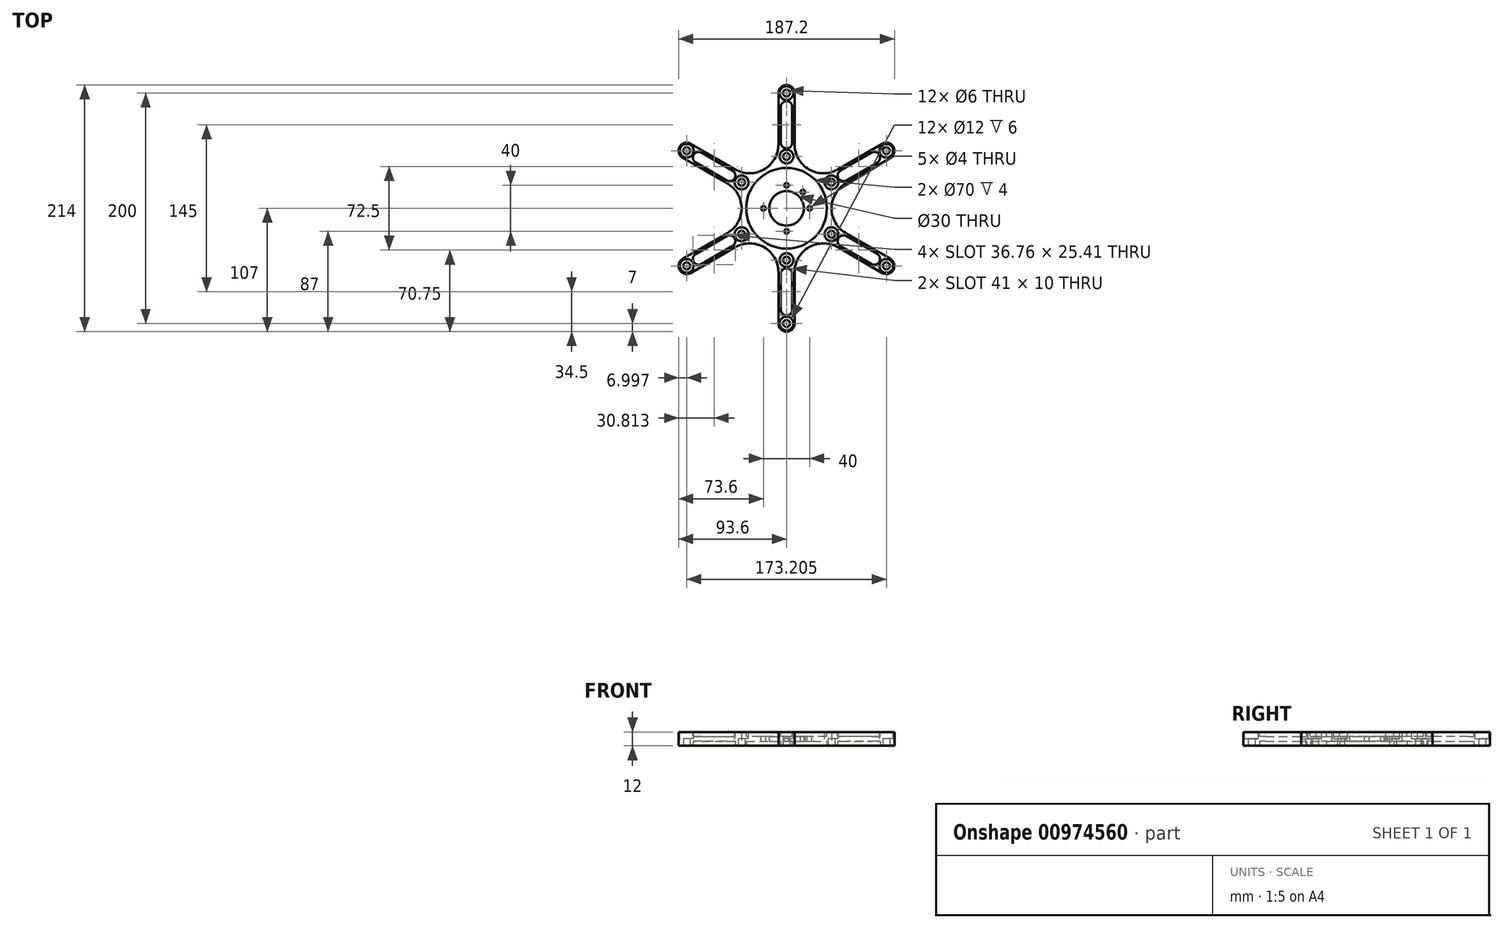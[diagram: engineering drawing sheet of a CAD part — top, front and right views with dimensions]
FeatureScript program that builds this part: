
annotation { "Feature Type Name" : "Feature", "Feature Type Description" : "" }
export const myFeature = defineFeature(function(context is Context, id is Id, definition is map)
    precondition{}
    {
        {
            var Q0;
            Q0=qCreatedBy(makeId("Top.planeOp"),FACE);
            var sketch = newSketch(context, id + "F0", { "sketchPlane" : qUnion([Q0])});
            skLineSegment(sketch, "E0", {"start": v(0, 0) * mm, "end": v(0, 90) * mm, "construction": true});
            skCircle(sketch, "E1", {"center": v(0, 100) * mm, "radius": 3 * mm});
            skCircle(sketch, "E2", {"center": v(0, 45) * mm, "radius": 3 * mm});
            skArc(sketch, "E3", {"start": v(7, 100) * mm, "mid": v(0, 107) * mm, "end": v(-7, 100) * mm});
            skLineSegment(sketch, "E4", {"start": v(-7, 100) * mm, "end": v(-7, 55.43) * mm});
            skLineSegment(sketch, "E5", {"start": v(7, 100) * mm, "end": v(7, 55.43) * mm});
            skLineSegment(sketch, "E6.1.0", {"start": v(-90.1, 43.94) * mm, "end": v(-51.5, 21.65) * mm});
            skCircle(sketch, "E6.1.1", {"center": v(-86.6, 50) * mm, "radius": 3 * mm});
            skCircle(sketch, "E6.1.2", {"center": v(-38.97, 22.5) * mm, "radius": 3 * mm});
            skArc(sketch, "E6.1.3", {"start": v(-83.1, 56.06) * mm, "mid": v(-92.66, 53.5) * mm, "end": v(-90.1, 43.94) * mm});
            skLineSegment(sketch, "E6.1.4", {"start": v(-83.1, 56.06) * mm, "end": v(-44.5, 33.77) * mm});
            skLineSegment(sketch, "E6.2.0", {"start": v(-83.1, -56.06) * mm, "end": v(-44.5, -33.77) * mm});
            skCircle(sketch, "E6.2.1", {"center": v(-86.6, -50) * mm, "radius": 3 * mm});
            skCircle(sketch, "E6.2.2", {"center": v(-38.97, -22.5) * mm, "radius": 3 * mm});
            skArc(sketch, "E6.2.3", {"start": v(-90.1, -43.94) * mm, "mid": v(-92.66, -53.5) * mm, "end": v(-83.1, -56.06) * mm});
            skLineSegment(sketch, "E6.2.4", {"start": v(-90.1, -43.94) * mm, "end": v(-51.5, -21.65) * mm});
            skLineSegment(sketch, "E6.3.0", {"start": v(7, -100) * mm, "end": v(7, -55.43) * mm});
            skCircle(sketch, "E6.3.1", {"center": v(0, -100) * mm, "radius": 3 * mm});
            skCircle(sketch, "E6.3.2", {"center": v(0, -45) * mm, "radius": 3 * mm});
            skArc(sketch, "E6.3.3", {"start": v(-7, -100) * mm, "mid": v(0, -107) * mm, "end": v(7, -100) * mm});
            skLineSegment(sketch, "E6.3.4", {"start": v(-7, -100) * mm, "end": v(-7, -55.43) * mm});
            skLineSegment(sketch, "E6.4.0", {"start": v(90.1, -43.94) * mm, "end": v(51.5, -21.65) * mm});
            skCircle(sketch, "E6.4.1", {"center": v(86.6, -50) * mm, "radius": 3 * mm});
            skCircle(sketch, "E6.4.2", {"center": v(38.97, -22.5) * mm, "radius": 3 * mm});
            skArc(sketch, "E6.4.3", {"start": v(83.1, -56.06) * mm, "mid": v(92.66, -53.5) * mm, "end": v(90.1, -43.94) * mm});
            skLineSegment(sketch, "E6.4.4", {"start": v(83.1, -56.06) * mm, "end": v(44.5, -33.77) * mm});
            skLineSegment(sketch, "E6.5.0", {"start": v(83.1, 56.06) * mm, "end": v(44.5, 33.77) * mm});
            skCircle(sketch, "E6.5.1", {"center": v(86.6, 50) * mm, "radius": 3 * mm});
            skCircle(sketch, "E6.5.2", {"center": v(38.97, 22.5) * mm, "radius": 3 * mm});
            skArc(sketch, "E6.5.3", {"start": v(90.1, 43.94) * mm, "mid": v(92.66, 53.5) * mm, "end": v(83.1, 56.06) * mm});
            skLineSegment(sketch, "E6.5.4", {"start": v(90.1, 43.94) * mm, "end": v(51.5, 21.65) * mm});
            skPoint(sketch, "E6.center", {"position": v(0, 0) * mm});
            skArc(sketch, "E7", {"start": v(7, 55.43) * mm, "mid": v(19.5, 33.77) * mm, "end": v(44.5, 33.77) * mm});
            skArc(sketch, "E8", {"start": v(-44.5, 33.77) * mm, "mid": v(-19.5, 33.77) * mm, "end": v(-7, 55.43) * mm});
            skArc(sketch, "E9", {"start": v(-51.5, -21.65) * mm, "mid": v(-39, 0) * mm, "end": v(-51.5, 21.65) * mm});
            skArc(sketch, "E10", {"start": v(-7, -55.43) * mm, "mid": v(-19.5, -33.77) * mm, "end": v(-44.5, -33.77) * mm});
            skArc(sketch, "E11", {"start": v(44.5, -33.77) * mm, "mid": v(19.5, -33.77) * mm, "end": v(7, -55.43) * mm});
            skArc(sketch, "E12", {"start": v(51.5, 21.65) * mm, "mid": v(39, 0) * mm, "end": v(51.5, -21.65) * mm});
            skLineSegment(sketch, "E13.trimOffspring", {"start": v(7, 12.12) * mm, "end": v(4.3, 10.57) * mm, "construction": true});
            skLineSegment(sketch, "E14.trimOffspring", {"start": v(7, 12.12) * mm, "end": v(7, 11.88) * mm, "construction": true});
            skLineSegment(sketch, "E15.trimOffspring", {"start": v(-7, 12.12) * mm, "end": v(-7, 9) * mm, "construction": true});
            skLineSegment(sketch, "E16.trimOffspring", {"start": v(-7, 12.12) * mm, "end": v(-6.8, 12) * mm, "construction": true});
            skLineSegment(sketch, "E17.trimOffspring", {"start": v(-14, 0) * mm, "end": v(-11.3, -1.56) * mm, "construction": true});
            skLineSegment(sketch, "E18.trimOffspring", {"start": v(-14, 0) * mm, "end": v(-13.8, 0.12) * mm, "construction": true});
            skLineSegment(sketch, "E19.trimOffspring", {"start": v(-7, -12.12) * mm, "end": v(-4.3, -10.57) * mm, "construction": true});
            skLineSegment(sketch, "E20.trimOffspring", {"start": v(-7, -12.12) * mm, "end": v(-7, -11.88) * mm, "construction": true});
            skLineSegment(sketch, "E21.trimOffspring", {"start": v(7, -12.12) * mm, "end": v(7, -9) * mm, "construction": true});
            skLineSegment(sketch, "E22.trimOffspring", {"start": v(7, -12.12) * mm, "end": v(6.8, -12) * mm, "construction": true});
            skLineSegment(sketch, "E23.trimOffspring", {"start": v(14, 0) * mm, "end": v(11.3, 1.56) * mm, "construction": true});
            skLineSegment(sketch, "E24.trimOffspring", {"start": v(14, 0) * mm, "end": v(13.8, -0.12) * mm, "construction": true});
            skCircle(sketch, "E25", {"center": v(0, 0) * mm, "radius": 15 * mm});
            skSolve(sketch);
        }
        {
            var Q0;
            Q0=qSketchRegion(id+"F0",true);
            extrude(context, id + "F1", {"entities" : qUnion([Q0]), "depth" : 12 * mm, "offsetDistance" : 25 * mm});
        }
        {
            var Q0;
            Q0=makeQuery(id+"F1.opExtrude","CAP_FACE",FACE,{"disambiguationData":[OSD([sQuery(id+"F0.wireOp",EDGE,"E1"),sQuery(id+"F0.wireOp",EDGE,"E2"),sQuery(id+"F0.wireOp",EDGE,"E3"),sQuery(id+"F0.wireOp",EDGE,"E4"),sQuery(id+"F0.wireOp",EDGE,"E5"),sQuery(id+"F0.wireOp",EDGE,"E6.1.0"),sQuery(id+"F0.wireOp",EDGE,"E6.1.1"),sQuery(id+"F0.wireOp",EDGE,"E6.1.2"),sQuery(id+"F0.wireOp",EDGE,"E6.1.3"),sQuery(id+"F0.wireOp",EDGE,"E6.1.4"),sQuery(id+"F0.wireOp",EDGE,"E6.2.0"),sQuery(id+"F0.wireOp",EDGE,"E6.2.1"),sQuery(id+"F0.wireOp",EDGE,"E6.2.2"),sQuery(id+"F0.wireOp",EDGE,"E6.2.3"),sQuery(id+"F0.wireOp",EDGE,"E6.2.4"),sQuery(id+"F0.wireOp",EDGE,"E6.3.0"),sQuery(id+"F0.wireOp",EDGE,"E6.3.1"),sQuery(id+"F0.wireOp",EDGE,"E6.3.2"),sQuery(id+"F0.wireOp",EDGE,"E6.3.3"),sQuery(id+"F0.wireOp",EDGE,"E6.3.4"),sQuery(id+"F0.wireOp",EDGE,"E6.4.0"),sQuery(id+"F0.wireOp",EDGE,"E6.4.1"),sQuery(id+"F0.wireOp",EDGE,"E6.4.2"),sQuery(id+"F0.wireOp",EDGE,"E6.4.3"),sQuery(id+"F0.wireOp",EDGE,"E6.4.4"),sQuery(id+"F0.wireOp",EDGE,"E6.5.0"),sQuery(id+"F0.wireOp",EDGE,"E6.5.1"),sQuery(id+"F0.wireOp",EDGE,"E6.5.2"),sQuery(id+"F0.wireOp",EDGE,"E6.5.3"),sQuery(id+"F0.wireOp",EDGE,"E6.5.4"),sQuery(id+"F0.wireOp",EDGE,"E7"),sQuery(id+"F0.wireOp",EDGE,"E8"),sQuery(id+"F0.wireOp",EDGE,"E9"),sQuery(id+"F0.wireOp",EDGE,"E10"),sQuery(id+"F0.wireOp",EDGE,"E11"),sQuery(id+"F0.wireOp",EDGE,"E12")])],"isStart":false});
            var sketch = newSketch(context, id + "F2", { "sketchPlane" : qUnion([Q0])});
            skCircle(sketch, "E26", {"center": v(-86.6, 50) * mm, "radius": 6 * mm});
            skCircle(sketch, "E27", {"center": v(0, 100) * mm, "radius": 6 * mm});
            skCircle(sketch, "E28", {"center": v(86.6, 50) * mm, "radius": 6 * mm});
            skCircle(sketch, "E29", {"center": v(86.6, -50) * mm, "radius": 6 * mm});
            skCircle(sketch, "E30", {"center": v(0, -100) * mm, "radius": 6 * mm});
            skCircle(sketch, "E31", {"center": v(-86.6, -50) * mm, "radius": 6 * mm});
            skCircle(sketch, "E32", {"center": v(-38.97, 22.5) * mm, "radius": 6 * mm});
            skCircle(sketch, "E33", {"center": v(0, 45) * mm, "radius": 6 * mm});
            skCircle(sketch, "E34", {"center": v(38.97, 22.5) * mm, "radius": 6 * mm});
            skCircle(sketch, "E35", {"center": v(38.97, -22.5) * mm, "radius": 6 * mm});
            skCircle(sketch, "E36", {"center": v(0, -45) * mm, "radius": 6 * mm});
            skCircle(sketch, "E37", {"center": v(-38.97, -22.5) * mm, "radius": 6 * mm});
            skSolve(sketch);
        }
        {
            var Q0;
            Q0 = qSketchRegion(id + "F2", true);
            extrude(context, id + "F3", {"entities" : qUnion([Q0]), "operationType" : NewBodyOperationType.REMOVE, "oppositeDirection" : true, "depth" : 6 * mm, "offsetDistance" : 25 * mm});
        }
        {
            var Q0;
            Q0=makeQuery(id+"F1.opExtrude","CAP_FACE",FACE,{"disambiguationData":[OSD([sQuery(id+"F0.wireOp",EDGE,"E1"),sQuery(id+"F0.wireOp",EDGE,"E2"),sQuery(id+"F0.wireOp",EDGE,"E3"),sQuery(id+"F0.wireOp",EDGE,"E4"),sQuery(id+"F0.wireOp",EDGE,"E5"),sQuery(id+"F0.wireOp",EDGE,"E6.1.0"),sQuery(id+"F0.wireOp",EDGE,"E6.1.1"),sQuery(id+"F0.wireOp",EDGE,"E6.1.2"),sQuery(id+"F0.wireOp",EDGE,"E6.1.3"),sQuery(id+"F0.wireOp",EDGE,"E6.1.4"),sQuery(id+"F0.wireOp",EDGE,"E6.2.0"),sQuery(id+"F0.wireOp",EDGE,"E6.2.1"),sQuery(id+"F0.wireOp",EDGE,"E6.2.2"),sQuery(id+"F0.wireOp",EDGE,"E6.2.3"),sQuery(id+"F0.wireOp",EDGE,"E6.2.4"),sQuery(id+"F0.wireOp",EDGE,"E6.3.0"),sQuery(id+"F0.wireOp",EDGE,"E6.3.1"),sQuery(id+"F0.wireOp",EDGE,"E6.3.2"),sQuery(id+"F0.wireOp",EDGE,"E6.3.3"),sQuery(id+"F0.wireOp",EDGE,"E6.3.4"),sQuery(id+"F0.wireOp",EDGE,"E6.4.0"),sQuery(id+"F0.wireOp",EDGE,"E6.4.1"),sQuery(id+"F0.wireOp",EDGE,"E6.4.2"),sQuery(id+"F0.wireOp",EDGE,"E6.4.3"),sQuery(id+"F0.wireOp",EDGE,"E6.4.4"),sQuery(id+"F0.wireOp",EDGE,"E6.5.0"),sQuery(id+"F0.wireOp",EDGE,"E6.5.1"),sQuery(id+"F0.wireOp",EDGE,"E6.5.2"),sQuery(id+"F0.wireOp",EDGE,"E6.5.3"),sQuery(id+"F0.wireOp",EDGE,"E6.5.4"),sQuery(id+"F0.wireOp",EDGE,"E7"),sQuery(id+"F0.wireOp",EDGE,"E8"),sQuery(id+"F0.wireOp",EDGE,"E9"),sQuery(id+"F0.wireOp",EDGE,"E10"),sQuery(id+"F0.wireOp",EDGE,"E11"),sQuery(id+"F0.wireOp",EDGE,"E12"),sQuery(id+"F0.wireOp",EDGE,"E25")])],"isStart":false});
            var sketch = newSketch(context, id + "F4", { "sketchPlane" : qUnion([Q0])});
            skCircle(sketch, "E38", {"center": v(0, 20) * mm, "radius": 2 * mm});
            skCircle(sketch, "E39.1.0", {"center": v(-20, 0) * mm, "radius": 2 * mm});
            skCircle(sketch, "E39.2.0", {"center": v(0, -20) * mm, "radius": 2 * mm});
            skCircle(sketch, "E39.3.0", {"center": v(20, 0) * mm, "radius": 2 * mm});
            skPoint(sketch, "E39.center", {"position": v(0, 0) * mm});
            skSolve(sketch);
        }
        {
            var Q0;
            Q0 = qSketchRegion(id + "F4", true);
            extrude(context, id + "F5", {"entities" : qUnion([Q0]), "operationType" : NewBodyOperationType.REMOVE, "endBound" : BoundingType.THROUGH_ALL, "oppositeDirection" : true, "depth" : 25 * mm, "offsetDistance" : 25 * mm});
        }
        {
            var Q0;
            Q0=makeQuery(id+"F1.opExtrude","CAP_FACE",FACE,{"disambiguationData":[OSD([sQuery(id+"F0.wireOp",EDGE,"E1"),sQuery(id+"F0.wireOp",EDGE,"E2"),sQuery(id+"F0.wireOp",EDGE,"E3"),sQuery(id+"F0.wireOp",EDGE,"E4"),sQuery(id+"F0.wireOp",EDGE,"E5"),sQuery(id+"F0.wireOp",EDGE,"E6.1.0"),sQuery(id+"F0.wireOp",EDGE,"E6.1.1"),sQuery(id+"F0.wireOp",EDGE,"E6.1.2"),sQuery(id+"F0.wireOp",EDGE,"E6.1.3"),sQuery(id+"F0.wireOp",EDGE,"E6.1.4"),sQuery(id+"F0.wireOp",EDGE,"E6.2.0"),sQuery(id+"F0.wireOp",EDGE,"E6.2.1"),sQuery(id+"F0.wireOp",EDGE,"E6.2.2"),sQuery(id+"F0.wireOp",EDGE,"E6.2.3"),sQuery(id+"F0.wireOp",EDGE,"E6.2.4"),sQuery(id+"F0.wireOp",EDGE,"E6.3.0"),sQuery(id+"F0.wireOp",EDGE,"E6.3.1"),sQuery(id+"F0.wireOp",EDGE,"E6.3.2"),sQuery(id+"F0.wireOp",EDGE,"E6.3.3"),sQuery(id+"F0.wireOp",EDGE,"E6.3.4"),sQuery(id+"F0.wireOp",EDGE,"E6.4.0"),sQuery(id+"F0.wireOp",EDGE,"E6.4.1"),sQuery(id+"F0.wireOp",EDGE,"E6.4.2"),sQuery(id+"F0.wireOp",EDGE,"E6.4.3"),sQuery(id+"F0.wireOp",EDGE,"E6.4.4"),sQuery(id+"F0.wireOp",EDGE,"E6.5.0"),sQuery(id+"F0.wireOp",EDGE,"E6.5.1"),sQuery(id+"F0.wireOp",EDGE,"E6.5.2"),sQuery(id+"F0.wireOp",EDGE,"E6.5.3"),sQuery(id+"F0.wireOp",EDGE,"E6.5.4"),sQuery(id+"F0.wireOp",EDGE,"E7"),sQuery(id+"F0.wireOp",EDGE,"E8"),sQuery(id+"F0.wireOp",EDGE,"E9"),sQuery(id+"F0.wireOp",EDGE,"E10"),sQuery(id+"F0.wireOp",EDGE,"E11"),sQuery(id+"F0.wireOp",EDGE,"E12"),sQuery(id+"F0.wireOp",EDGE,"E25")])],"isStart":false});
            var sketch = newSketch(context, id + "F6", { "sketchPlane" : qUnion([Q0])});
            skCircle(sketch, "E40", {"center": v(0, 0) * mm, "radius": 35 * mm});
            skLineSegment(sketch, "E41", {"start": v(0, 0) * mm, "end": v(0, 89.1) * mm, "construction": true});
            skLineSegment(sketch, "E42.bottom", {"start": v(0, 93) * mm, "end": v(0, 93) * mm});
            skLineSegment(sketch, "E42.top", {"start": v(0, 52) * mm, "end": v(0, 52) * mm});
            skLineSegment(sketch, "E42.left", {"start": v(-5, 88) * mm, "end": v(-5, 57) * mm});
            skLineSegment(sketch, "E42.right", {"start": v(5, 88) * mm, "end": v(5, 57) * mm});
            skLineSegment(sketch, "E43", {"start": v(-25.17, 72.5) * mm, "end": v(32.56, 72.5) * mm, "construction": true});
            skPoint(sketch, "E43.startSnap0", {"position": v(-5, 72.5) * mm});
            skPoint(sketch, "E44.visualSharp", {"position": v(-5, 93) * mm});
            skArc(sketch, "E44.filletArc", {"start": v(0, 93) * mm, "mid": v(-3.54, 91.54) * mm, "end": v(-5, 88) * mm});
            skPoint(sketch, "E45.visualSharp", {"position": v(5, 52) * mm});
            skArc(sketch, "E45.filletArc", {"start": v(0, 52) * mm, "mid": v(3.54, 53.46) * mm, "end": v(5, 57) * mm});
            skPoint(sketch, "E46.visualSharp", {"position": v(-5, 52) * mm});
            skArc(sketch, "E46.filletArc", {"start": v(-5, 57) * mm, "mid": v(-3.54, 53.46) * mm, "end": v(0, 52) * mm});
            skPoint(sketch, "E47.visualSharp", {"position": v(5, 93) * mm});
            skArc(sketch, "E47.filletArc", {"start": v(5, 88) * mm, "mid": v(3.54, 91.54) * mm, "end": v(0, 93) * mm});
            skPoint(sketch, "E48.1.0", {"position": v(-65.29, 31.92) * mm});
            skLineSegment(sketch, "E48.1.1", {"start": v(-73.71, 48.33) * mm, "end": v(-46.86, 32.83) * mm});
            skPoint(sketch, "E48.1.2", {"position": v(-47.53, 21.67) * mm});
            skPoint(sketch, "E48.1.3", {"position": v(-78.04, 50.83) * mm});
            skLineSegment(sketch, "E48.1.4", {"start": v(-78.71, 39.67) * mm, "end": v(-51.86, 24.17) * mm});
            skPoint(sketch, "E48.1.5", {"position": v(-42.53, 30.33) * mm});
            skPoint(sketch, "E48.1.6", {"position": v(-83.04, 42.17) * mm});
            skArc(sketch, "E48.1.7", {"start": v(-51.86, 24.17) * mm, "mid": v(-48.07, 23.67) * mm, "end": v(-45.03, 26) * mm});
            skArc(sketch, "E48.1.8", {"start": v(-45.03, 26) * mm, "mid": v(-44.53, 29.8) * mm, "end": v(-46.86, 32.83) * mm});
            skArc(sketch, "E48.1.9", {"start": v(-80.54, 46.5) * mm, "mid": v(-81.04, 42.7) * mm, "end": v(-78.71, 39.67) * mm});
            skArc(sketch, "E48.1.10", {"start": v(-73.71, 48.33) * mm, "mid": v(-77.5, 48.83) * mm, "end": v(-80.54, 46.5) * mm});
            skPoint(sketch, "E48.2.0", {"position": v(-60.29, -40.58) * mm});
            skLineSegment(sketch, "E48.2.1", {"start": v(-78.71, -39.67) * mm, "end": v(-51.86, -24.17) * mm});
            skPoint(sketch, "E48.2.2", {"position": v(-42.53, -30.33) * mm});
            skPoint(sketch, "E48.2.3", {"position": v(-83.04, -42.17) * mm});
            skLineSegment(sketch, "E48.2.4", {"start": v(-73.71, -48.33) * mm, "end": v(-46.86, -32.83) * mm});
            skPoint(sketch, "E48.2.5", {"position": v(-47.53, -21.67) * mm});
            skPoint(sketch, "E48.2.6", {"position": v(-78.04, -50.83) * mm});
            skArc(sketch, "E48.2.7", {"start": v(-46.86, -32.83) * mm, "mid": v(-44.53, -29.8) * mm, "end": v(-45.03, -26) * mm});
            skArc(sketch, "E48.2.8", {"start": v(-45.03, -26) * mm, "mid": v(-48.07, -23.67) * mm, "end": v(-51.86, -24.17) * mm});
            skArc(sketch, "E48.2.9", {"start": v(-80.54, -46.5) * mm, "mid": v(-77.5, -48.83) * mm, "end": v(-73.71, -48.33) * mm});
            skArc(sketch, "E48.2.10", {"start": v(-78.71, -39.67) * mm, "mid": v(-81.04, -42.7) * mm, "end": v(-80.54, -46.5) * mm});
            skPoint(sketch, "E48.3.0", {"position": v(5, -72.5) * mm});
            skLineSegment(sketch, "E48.3.1", {"start": v(-5, -88) * mm, "end": v(-5, -57) * mm});
            skPoint(sketch, "E48.3.2", {"position": v(5, -52) * mm});
            skPoint(sketch, "E48.3.3", {"position": v(-5, -93) * mm});
            skLineSegment(sketch, "E48.3.4", {"start": v(5, -88) * mm, "end": v(5, -57) * mm});
            skPoint(sketch, "E48.3.5", {"position": v(-5, -52) * mm});
            skPoint(sketch, "E48.3.6", {"position": v(5, -93) * mm});
            skArc(sketch, "E48.3.7", {"start": v(5, -57) * mm, "mid": v(3.54, -53.46) * mm, "end": v(0, -52) * mm});
            skArc(sketch, "E48.3.8", {"start": v(0, -52) * mm, "mid": v(-3.54, -53.46) * mm, "end": v(-5, -57) * mm});
            skArc(sketch, "E48.3.9", {"start": v(0, -93) * mm, "mid": v(3.54, -91.54) * mm, "end": v(5, -88) * mm});
            skArc(sketch, "E48.3.10", {"start": v(-5, -88) * mm, "mid": v(-3.54, -91.54) * mm, "end": v(0, -93) * mm});
            skPoint(sketch, "E48.4.0", {"position": v(65.29, -31.92) * mm});
            skLineSegment(sketch, "E48.4.1", {"start": v(73.71, -48.33) * mm, "end": v(46.86, -32.83) * mm});
            skPoint(sketch, "E48.4.2", {"position": v(47.53, -21.67) * mm});
            skPoint(sketch, "E48.4.3", {"position": v(78.04, -50.83) * mm});
            skLineSegment(sketch, "E48.4.4", {"start": v(78.71, -39.67) * mm, "end": v(51.86, -24.17) * mm});
            skPoint(sketch, "E48.4.5", {"position": v(42.53, -30.33) * mm});
            skPoint(sketch, "E48.4.6", {"position": v(83.04, -42.17) * mm});
            skArc(sketch, "E48.4.7", {"start": v(51.86, -24.17) * mm, "mid": v(48.07, -23.67) * mm, "end": v(45.03, -26) * mm});
            skArc(sketch, "E48.4.8", {"start": v(45.03, -26) * mm, "mid": v(44.53, -29.8) * mm, "end": v(46.86, -32.83) * mm});
            skArc(sketch, "E48.4.9", {"start": v(80.54, -46.5) * mm, "mid": v(81.04, -42.7) * mm, "end": v(78.71, -39.67) * mm});
            skArc(sketch, "E48.4.10", {"start": v(73.71, -48.33) * mm, "mid": v(77.5, -48.83) * mm, "end": v(80.54, -46.5) * mm});
            skPoint(sketch, "E48.5.0", {"position": v(60.29, 40.58) * mm});
            skLineSegment(sketch, "E48.5.1", {"start": v(78.71, 39.67) * mm, "end": v(51.86, 24.17) * mm});
            skPoint(sketch, "E48.5.2", {"position": v(42.53, 30.33) * mm});
            skPoint(sketch, "E48.5.3", {"position": v(83.04, 42.17) * mm});
            skLineSegment(sketch, "E48.5.4", {"start": v(73.71, 48.33) * mm, "end": v(46.86, 32.83) * mm});
            skPoint(sketch, "E48.5.5", {"position": v(47.53, 21.67) * mm});
            skPoint(sketch, "E48.5.6", {"position": v(78.04, 50.83) * mm});
            skArc(sketch, "E48.5.7", {"start": v(46.86, 32.83) * mm, "mid": v(44.53, 29.8) * mm, "end": v(45.03, 26) * mm});
            skArc(sketch, "E48.5.8", {"start": v(45.03, 26) * mm, "mid": v(48.07, 23.67) * mm, "end": v(51.86, 24.17) * mm});
            skArc(sketch, "E48.5.9", {"start": v(80.54, 46.5) * mm, "mid": v(77.5, 48.83) * mm, "end": v(73.71, 48.33) * mm});
            skArc(sketch, "E48.5.10", {"start": v(78.71, 39.67) * mm, "mid": v(81.04, 42.7) * mm, "end": v(80.54, 46.5) * mm});
            skSolve(sketch);
        }
        {
            var Q0;
            Q0 = qSketchRegion(id + "F6", true);
            extrude(context, id + "F7", {"entities" : qUnion([Q0]), "operationType" : NewBodyOperationType.REMOVE, "oppositeDirection" : true, "depth" : 4 * mm, "offsetDistance" : 25 * mm});
        }
        {
            var Q0;
            Q0=makeQuery(id+"F1.opExtrude","CAP_FACE",FACE,{"disambiguationData":[OSD([sQuery(id+"F0.wireOp",EDGE,"E1"),sQuery(id+"F0.wireOp",EDGE,"E2"),sQuery(id+"F0.wireOp",EDGE,"E3"),sQuery(id+"F0.wireOp",EDGE,"E4"),sQuery(id+"F0.wireOp",EDGE,"E5"),sQuery(id+"F0.wireOp",EDGE,"E6.1.0"),sQuery(id+"F0.wireOp",EDGE,"E6.1.1"),sQuery(id+"F0.wireOp",EDGE,"E6.1.2"),sQuery(id+"F0.wireOp",EDGE,"E6.1.3"),sQuery(id+"F0.wireOp",EDGE,"E6.1.4"),sQuery(id+"F0.wireOp",EDGE,"E6.2.0"),sQuery(id+"F0.wireOp",EDGE,"E6.2.1"),sQuery(id+"F0.wireOp",EDGE,"E6.2.2"),sQuery(id+"F0.wireOp",EDGE,"E6.2.3"),sQuery(id+"F0.wireOp",EDGE,"E6.2.4"),sQuery(id+"F0.wireOp",EDGE,"E6.3.0"),sQuery(id+"F0.wireOp",EDGE,"E6.3.1"),sQuery(id+"F0.wireOp",EDGE,"E6.3.2"),sQuery(id+"F0.wireOp",EDGE,"E6.3.3"),sQuery(id+"F0.wireOp",EDGE,"E6.3.4"),sQuery(id+"F0.wireOp",EDGE,"E6.4.0"),sQuery(id+"F0.wireOp",EDGE,"E6.4.1"),sQuery(id+"F0.wireOp",EDGE,"E6.4.2"),sQuery(id+"F0.wireOp",EDGE,"E6.4.3"),sQuery(id+"F0.wireOp",EDGE,"E6.4.4"),sQuery(id+"F0.wireOp",EDGE,"E6.5.0"),sQuery(id+"F0.wireOp",EDGE,"E6.5.1"),sQuery(id+"F0.wireOp",EDGE,"E6.5.2"),sQuery(id+"F0.wireOp",EDGE,"E6.5.3"),sQuery(id+"F0.wireOp",EDGE,"E6.5.4"),sQuery(id+"F0.wireOp",EDGE,"E7"),sQuery(id+"F0.wireOp",EDGE,"E8"),sQuery(id+"F0.wireOp",EDGE,"E9"),sQuery(id+"F0.wireOp",EDGE,"E10"),sQuery(id+"F0.wireOp",EDGE,"E11"),sQuery(id+"F0.wireOp",EDGE,"E12"),sQuery(id+"F0.wireOp",EDGE,"E25")])],"isStart":true});
            var sketch = newSketch(context, id + "F8", { "sketchPlane" : qUnion([Q0])});
            skCircle(sketch, "E49.0.0", {"center": v(0, 0) * mm, "radius": 35 * mm});
            skArc(sketch, "E50.0.0", {"start": v(-78.71, 39.67) * mm, "mid": v(-80.54, 46.5) * mm, "end": v(-73.71, 48.33) * mm});
            skLineSegment(sketch, "E50.0.1", {"start": v(-73.71, 48.33) * mm, "end": v(-46.86, 32.83) * mm});
            skArc(sketch, "E50.0.2", {"start": v(-46.86, 32.83) * mm, "mid": v(-45.03, 26) * mm, "end": v(-51.86, 24.17) * mm});
            skLineSegment(sketch, "E50.0.3", {"start": v(-51.86, 24.17) * mm, "end": v(-78.71, 39.67) * mm});
            skArc(sketch, "E51.0.0", {"start": v(-73.71, -48.33) * mm, "mid": v(-80.54, -46.5) * mm, "end": v(-78.71, -39.67) * mm});
            skLineSegment(sketch, "E51.0.1", {"start": v(-78.71, -39.67) * mm, "end": v(-51.86, -24.17) * mm});
            skArc(sketch, "E51.0.2", {"start": v(-51.86, -24.17) * mm, "mid": v(-45.03, -26) * mm, "end": v(-46.86, -32.83) * mm});
            skLineSegment(sketch, "E51.0.3", {"start": v(-46.86, -32.83) * mm, "end": v(-73.71, -48.33) * mm});
            skArc(sketch, "E52.0.0", {"start": v(-5, -57) * mm, "mid": v(0, -52) * mm, "end": v(5, -57) * mm});
            skLineSegment(sketch, "E52.0.1", {"start": v(5, -57) * mm, "end": v(5, -88) * mm});
            skArc(sketch, "E52.0.2", {"start": v(5, -88) * mm, "mid": v(0, -93) * mm, "end": v(-5, -88) * mm});
            skLineSegment(sketch, "E52.0.3", {"start": v(-5, -88) * mm, "end": v(-5, -57) * mm});
            skArc(sketch, "E53.0.0", {"start": v(78.71, -39.67) * mm, "mid": v(80.54, -46.5) * mm, "end": v(73.71, -48.33) * mm});
            skLineSegment(sketch, "E53.0.1", {"start": v(73.71, -48.33) * mm, "end": v(46.86, -32.83) * mm});
            skArc(sketch, "E53.0.2", {"start": v(46.86, -32.83) * mm, "mid": v(45.03, -26) * mm, "end": v(51.86, -24.17) * mm});
            skLineSegment(sketch, "E53.0.3", {"start": v(51.86, -24.17) * mm, "end": v(78.71, -39.67) * mm});
            skArc(sketch, "E54.0.0", {"start": v(73.71, 48.33) * mm, "mid": v(80.54, 46.5) * mm, "end": v(78.71, 39.67) * mm});
            skLineSegment(sketch, "E54.0.1", {"start": v(78.71, 39.67) * mm, "end": v(51.86, 24.17) * mm});
            skArc(sketch, "E54.0.2", {"start": v(51.86, 24.17) * mm, "mid": v(45.03, 26) * mm, "end": v(46.86, 32.83) * mm});
            skLineSegment(sketch, "E54.0.3", {"start": v(46.86, 32.83) * mm, "end": v(73.71, 48.33) * mm});
            skArc(sketch, "E55.0.0", {"start": v(-5, 88) * mm, "mid": v(0, 93) * mm, "end": v(5, 88) * mm});
            skLineSegment(sketch, "E55.0.1", {"start": v(5, 88) * mm, "end": v(5, 57) * mm});
            skArc(sketch, "E55.0.2", {"start": v(5, 57) * mm, "mid": v(0, 52) * mm, "end": v(-5, 57) * mm});
            skLineSegment(sketch, "E55.0.3", {"start": v(-5, 57) * mm, "end": v(-5, 88) * mm});
            skSolve(sketch);
        }
        {
            var Q0;
            Q0 = qSketchRegion(id + "F8", true);
            extrude(context, id + "F9", {"entities" : qUnion([Q0]), "operationType" : NewBodyOperationType.REMOVE, "oppositeDirection" : true, "depth" : 4 * mm, "offsetDistance" : 25 * mm});
        }
        {
            var Q0;
            Q0=makeQuery(id+"F7.boolean.opBoolean","COPY",FACE,{"derivedFrom":makeQuery(id+"F7.opExtrude","CAP_FACE",FACE,{"disambiguationData":[OSD([sQuery(id+"F6.wireOp",EDGE,"E40")])],"isStart":false})});
            var sketch = newSketch(context, id + "F10", { "sketchPlane" : qUnion([Q0])});
            skCircle(sketch, "E56", {"center": v(0, 0) * mm, "radius": 20 * mm, "construction": true});
            skLineSegment(sketch, "E57", {"start": v(0, 0) * mm, "end": v(45.22, 45.22) * mm, "construction": true});
            skCircle(sketch, "E58", {"center": v(14.14, 14.14) * mm, "radius": 2 * mm});
            skSolve(sketch);
        }
        {
            var Q0;
            Q0 = qSketchRegion(id + "F10", true);
            extrude(context, id + "F11", {"entities" : qUnion([Q0]), "operationType" : NewBodyOperationType.REMOVE, "oppositeDirection" : true, "depth" : 25 * mm, "offsetDistance" : 25 * mm});
        }
    });
